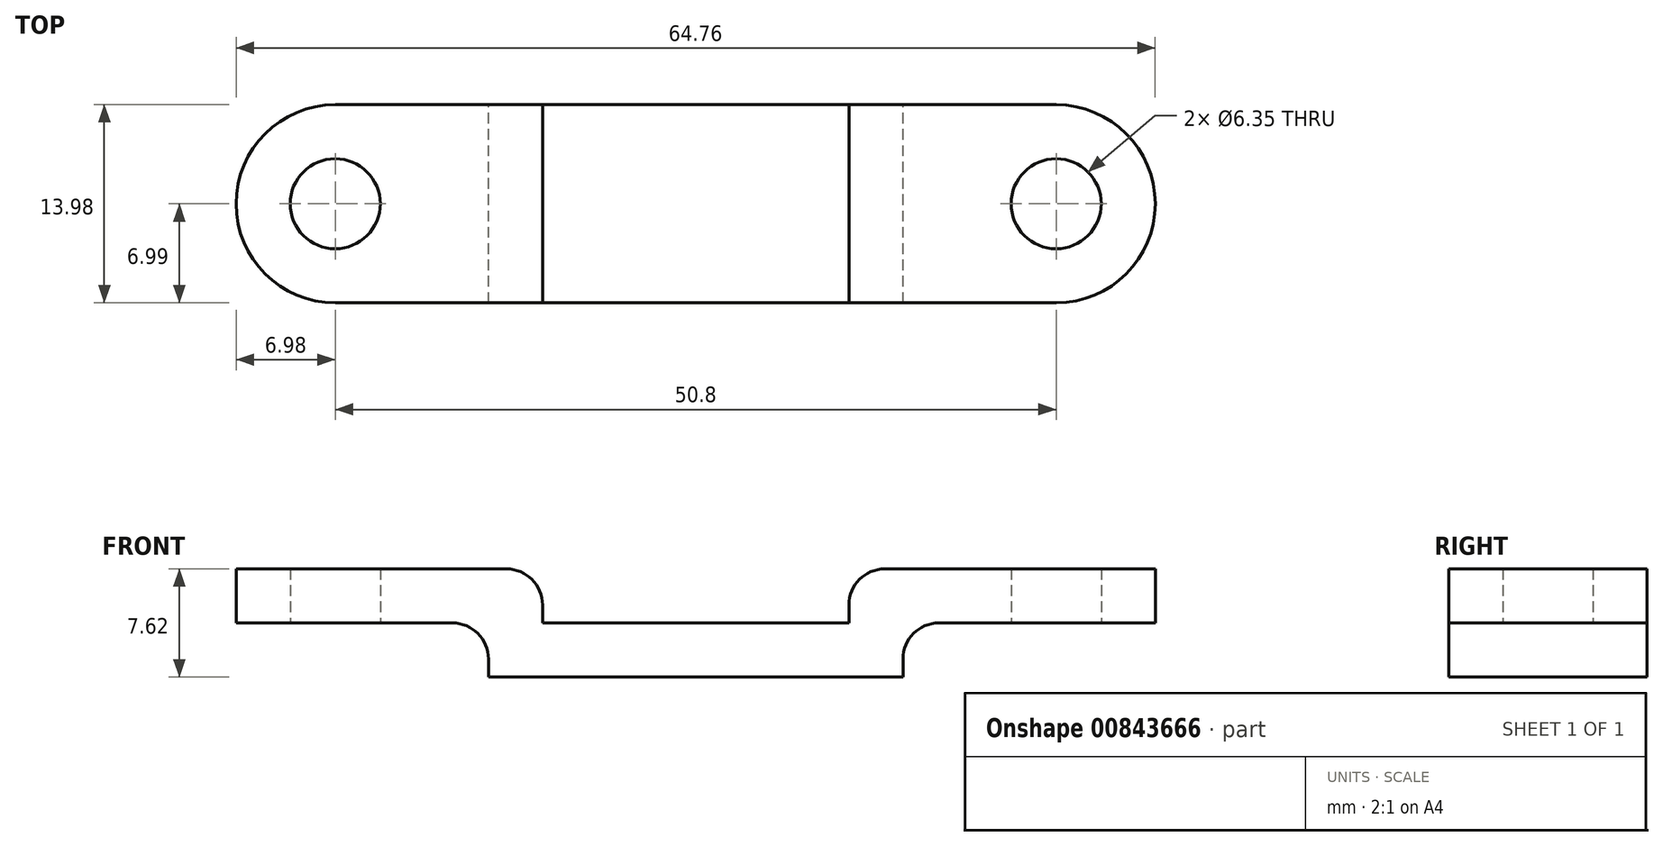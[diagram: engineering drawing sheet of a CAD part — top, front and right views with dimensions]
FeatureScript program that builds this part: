
annotation { "Feature Type Name" : "Feature", "Feature Type Description" : "" }
export const myFeature = defineFeature(function(context is Context, id is Id, definition is map)
    precondition{}
    {
        {
            var Q0;
            Q0=qCreatedBy(makeId("Top.planeOp"),FACE);
            var sketch = newSketch(context, id + "F0", { "sketchPlane" : qUnion([Q0])});
            skLineSegment(sketch, "E0.bottom", {"start": v(25.4, 6.99) * mm, "end": v(-25.4, 6.99) * mm});
            skLineSegment(sketch, "E0.top", {"start": v(25.4, -6.98) * mm, "end": v(-25.4, -6.98) * mm});
            skPoint(sketch, "E0.middle", {"position": v(0, 0) * mm});
            skArc(sketch, "E1", {"start": v(-25.4, 6.99) * mm, "mid": v(-32.38, 0) * mm, "end": v(-25.4, -6.98) * mm});
            skArc(sketch, "E2", {"start": v(25.4, -6.98) * mm, "mid": v(32.39, 0) * mm, "end": v(25.4, 6.99) * mm});
            skCircle(sketch, "E3", {"center": v(-25.4, 0) * mm, "radius": 3.18 * mm});
            skCircle(sketch, "E4", {"center": v(25.4, 0) * mm, "radius": 3.18 * mm});
            skLineSegment(sketch, "E5.bottom", {"start": v(-10.8, 6.99) * mm, "end": v(10.8, 6.99) * mm, "construction": true});
            skLineSegment(sketch, "E5.top", {"start": v(-10.8, -6.99) * mm, "end": v(10.8, -6.99) * mm, "construction": true});
            skLineSegment(sketch, "E5.left", {"start": v(-10.8, 6.99) * mm, "end": v(-10.8, -6.99) * mm, "construction": true});
            skLineSegment(sketch, "E5.right", {"start": v(10.8, 6.99) * mm, "end": v(10.8, -6.99) * mm, "construction": true});
            skSolve(sketch);
        }
        {
            var Q0;
            Q0 = qSketchRegion(id + "F0", true);
            extrude(context, id + "F1", {"entities" : qUnion([Q0]), "depth" : 7.62 * mm / 2, "offsetDistance" : 25.4 * mm});
        }
        {
            var Q0;
            Q0=makeQuery(id+"F1.opExtrude","CAP_FACE",FACE,{"disambiguationData":[OSD([sQuery(id+"F0.wireOp",EDGE,"E0.bottom"),sQuery(id+"F0.wireOp",EDGE,"E0.top"),sQuery(id+"F0.wireOp",EDGE,"E1"),sQuery(id+"F0.wireOp",EDGE,"E2"),sQuery(id+"F0.wireOp",EDGE,"E3"),sQuery(id+"F0.wireOp",EDGE,"E4")])],"isStart":false});
            var sketch = newSketch(context, id + "F2", { "sketchPlane" : qUnion([Q0])});
            skLineSegment(sketch, "E6.0", {"start": v(-10.8, 6.99) * mm, "end": v(-10.8, -6.99) * mm});
            skCircle(sketch, "E7.0", {"center": v(-25.4, 0) * mm, "radius": 3.18 * mm});
            skArc(sketch, "E8.0", {"start": v(-25.4, 6.99) * mm, "mid": v(-32.38, 0) * mm, "end": v(-25.4, -6.98) * mm});
            skLineSegment(sketch, "E9.0", {"start": v(-10.8, 6.99) * mm, "end": v(-25.4, 6.99) * mm});
            skLineSegment(sketch, "E10.0", {"start": v(-10.8, -6.98) * mm, "end": v(-25.4, -6.98) * mm});
            skSolve(sketch);
        }
        {
            var Q0;
            Q0=makeQuery(id+"F2.imprint","IMPRINT",FACE,{"disambiguationData":[TD([[makeQuery(id+"F2.imprint","IMPRINT",EDGE,{"derivedFrom":sQuery(id+"F2.wireOp",EDGE,"E6.0")}),-1.0]])]});
            extrude(context, id + "F3", {"entities" : qUnion([Q0]), "operationType" : NewBodyOperationType.ADD, "depth" : 7.62 * mm / 2, "offsetDistance" : 25.4 * mm});
        }
        {
            var Q0;
            Q0=makeQuery(id+"F3.boolean.opBoolean","MERGE",FACE,{"derivedFrom":[makeQuery(id+"F1.opExtrude","SWEPT_FACE",FACE,{"disambiguationData":[OSD([sQuery(id+"F0.wireOp",EDGE,"E0.bottom")])]}),makeQuery(id+"F3.opExtrude","SWEPT_FACE",FACE,{"disambiguationData":[OSD([sQuery(id+"F2.wireOp",EDGE,"E9.0")])]})]});
            var sketch = newSketch(context, id + "F4", { "sketchPlane" : qUnion([Q0])});
            skLineSegment(sketch, "E11.bottom", {"start": v(14.6, 0) * mm, "end": v(60.73, 0) * mm});
            skLineSegment(sketch, "E11.top", {"start": v(14.6, 3.81) * mm, "end": v(60.73, 3.81) * mm});
            skLineSegment(sketch, "E11.left", {"start": v(14.6, 0) * mm, "end": v(14.6, 3.81) * mm});
            skLineSegment(sketch, "E11.right", {"start": v(60.73, 0) * mm, "end": v(60.73, 3.81) * mm});
            skSolve(sketch);
        }
        {
            var Q0;
            {var subQ3=sQuery(id+"F4.wireOp",EDGE,"E11.right");Q0=makeQuery(id+"F4.imprint","IMPRINT",FACE,{"disambiguationData":[TD([[makeQuery(id+"F4.imprint","IMPRINT",EDGE,{"derivedFrom":subQ3}),1.0]])]});}
            var Q1;
            {var subQ4=sQuery(id+"F4.wireOp",EDGE,"E11.left");Q1=makeQuery(id+"F4.imprint","IMPRINT",FACE,{"disambiguationData":[TD([[makeQuery(id+"F4.imprint","IMPRINT",EDGE,{"derivedFrom":subQ4}),-1.0]])]});}
            extrude(context, id + "F5", {"entities" : qUnion([Q0, Q1]), "operationType" : NewBodyOperationType.REMOVE, "oppositeDirection" : true, "depth" : 38.1 * mm, "offsetDistance" : 25.4 * mm});
        }
        {
            var Q0;
            Q0=makeQuery(id+"F3.opExtrude","CAP_EDGE",EDGE,{"disambiguationData":[OSD([sQuery(id+"F2.wireOp",EDGE,"E6.0")])],"isStart":true});
            var Q1;
            Q1=makeQuery(id+"F5.boolean.opBoolean","COPY",EDGE,{"derivedFrom":makeQuery(id+"F5.opExtrude","SWEPT_EDGE",EDGE,{"disambiguationData":[OSD([sQuery(id+"F4.wireOp",EDGE,"E11.top"),sQuery(id+"F4.wireOp",EDGE,"E11.left")])]})});
            fillet(context, id + "F6", {"entities" : qUnion([Q0, Q1]), "radius" : 2.54 * mm, "tangentPropagation" : true, "allowEdgeOverflow" : false});
        }
        {
            var Q0;
            Q0=makeQuery(id+"F3.opExtrude","CAP_EDGE",EDGE,{"disambiguationData":[OSD([sQuery(id+"F2.wireOp",EDGE,"E6.0")])],"isStart":false});
            var Q1;
            Q1=makeQuery(id+"F5.boolean.opBoolean","COPY",EDGE,{"derivedFrom":makeQuery(id+"F5.opExtrude","SWEPT_EDGE",EDGE,{"disambiguationData":[OSD([sQuery(id+"F0.wireOp",EDGE,"E0.bottom"),sQuery(id+"F4.wireOp",EDGE,"E11.bottom"),sQuery(id+"F4.wireOp",EDGE,"E11.left")])]})});
            var Q2;
            Q2=makeQuery(id+"F6.opFillet","BLEND_EDGE",EDGE,{"blendedFrom":[makeQuery(id+"F5.boolean.opBoolean","COPY",EDGE,{"derivedFrom":makeQuery(id+"F5.opExtrude","SWEPT_EDGE",EDGE,{"disambiguationData":[OSD([sQuery(id+"F4.wireOp",EDGE,"E11.top"),sQuery(id+"F4.wireOp",EDGE,"E11.left")])]})}),makeQuery(id+"F1.opExtrude","CAP_FACE",FACE,{"disambiguationData":[OSD([sQuery(id+"F0.wireOp",EDGE,"E0.bottom"),sQuery(id+"F0.wireOp",EDGE,"E0.top"),sQuery(id+"F0.wireOp",EDGE,"E1"),sQuery(id+"F0.wireOp",EDGE,"E2"),sQuery(id+"F0.wireOp",EDGE,"E3"),sQuery(id+"F0.wireOp",EDGE,"E4")])],"isStart":true})],"blendedInto":[makeQuery(id+"F1.opExtrude","CAP_FACE",FACE,{"disambiguationData":[OSD([sQuery(id+"F0.wireOp",EDGE,"E0.bottom"),sQuery(id+"F0.wireOp",EDGE,"E0.top"),sQuery(id+"F0.wireOp",EDGE,"E1"),sQuery(id+"F0.wireOp",EDGE,"E2"),sQuery(id+"F0.wireOp",EDGE,"E3"),sQuery(id+"F0.wireOp",EDGE,"E4")])],"isStart":true})]});
            var Q3;
            {var subQ0=sQuery(id+"F2.wireOp",EDGE,"E6.0");Q3=makeQuery(id+"F6.opFillet","BLEND_EDGE",EDGE,{"blendedFrom":[makeQuery(id+"F3.opExtrude","CAP_EDGE",EDGE,{"disambiguationData":[OSD([subQ0])],"isStart":true}),makeQuery(id+"F3.opExtrude","CAP_FACE",FACE,{"disambiguationData":[OSD([subQ0,sQuery(id+"F2.wireOp",EDGE,"E7.0"),sQuery(id+"F2.wireOp",EDGE,"E8.0"),sQuery(id+"F2.wireOp",EDGE,"E9.0"),sQuery(id+"F2.wireOp",EDGE,"E10.0")])],"isStart":false})],"blendedInto":[makeQuery(id+"F3.opExtrude","CAP_FACE",FACE,{"disambiguationData":[OSD([subQ0,sQuery(id+"F2.wireOp",EDGE,"E7.0"),sQuery(id+"F2.wireOp",EDGE,"E8.0"),sQuery(id+"F2.wireOp",EDGE,"E9.0"),sQuery(id+"F2.wireOp",EDGE,"E10.0")])],"isStart":false})]});}
            fillet(context, id + "F7", {"entities" : qUnion([Q0, Q1, Q2, Q3]), "radius" : 2.54 * mm, "tangentPropagation" : true, "allowEdgeOverflow" : false});
        }
        {
            var Q0;
            Q0=makeQuery(id+"F1.opExtrude","CAP_FACE",FACE,{"disambiguationData":[OSD([sQuery(id+"F0.wireOp",EDGE,"E0.bottom"),sQuery(id+"F0.wireOp",EDGE,"E0.top"),sQuery(id+"F0.wireOp",EDGE,"E1"),sQuery(id+"F0.wireOp",EDGE,"E2"),sQuery(id+"F0.wireOp",EDGE,"E3"),sQuery(id+"F0.wireOp",EDGE,"E4")])],"isStart":false});
            var sketch = newSketch(context, id + "F8", { "sketchPlane" : qUnion([Q0])});
            skLineSegment(sketch, "E12.0", {"start": v(10.8, 6.99) * mm, "end": v(10.8, -6.99) * mm});
            skLineSegment(sketch, "E13.0.0", {"start": v(25.4, 6.99) * mm, "end": v(10.8, 6.99) * mm});
            skLineSegment(sketch, "E13.0.2", {"start": v(10.8, -6.98) * mm, "end": v(25.4, -6.98) * mm});
            skArc(sketch, "E13.0.3", {"start": v(25.4, -6.98) * mm, "mid": v(32.39, 0) * mm, "end": v(25.4, 6.99) * mm});
            skCircle(sketch, "E14.0", {"center": v(25.4, 0) * mm, "radius": 3.18 * mm});
            skPoint(sketch, "E13.0.1.end.orphan", {"position": v(-8.26, -6.98) * mm});
            skPoint(sketch, "E13.0.1.start.orphan", {"position": v(-8.26, 6.99) * mm});
            skSolve(sketch);
        }
        {
            var Q0;
            Q0 = qSketchRegion(id + "F8", true);
            extrude(context, id + "F9", {"entities" : qUnion([Q0]), "operationType" : NewBodyOperationType.ADD, "depth" : 7.62 * mm / 2, "offsetDistance" : 25.4 * mm});
        }
        {
            var Q0;
            Q0=makeQuery(id+"F9.boolean.opBoolean","MERGE",FACE,{"derivedFrom":[makeQuery(id+"F3.boolean.opBoolean","MERGE",FACE,{"derivedFrom":[makeQuery(id+"F1.opExtrude","SWEPT_FACE",FACE,{"disambiguationData":[OSD([sQuery(id+"F0.wireOp",EDGE,"E0.bottom")])]}),makeQuery(id+"F3.opExtrude","SWEPT_FACE",FACE,{"disambiguationData":[OSD([sQuery(id+"F2.wireOp",EDGE,"E9.0")])]})]}),makeQuery(id+"F9.opExtrude","SWEPT_FACE",FACE,{"disambiguationData":[OSD([sQuery(id+"F8.wireOp",EDGE,"E13.0.0")])]})]});
            var sketch = newSketch(context, id + "F10", { "sketchPlane" : qUnion([Q0])});
            skLineSegment(sketch, "E15.bottom", {"start": v(-14.6, 0) * mm, "end": v(-33.66, 0) * mm});
            skLineSegment(sketch, "E15.top", {"start": v(-14.6, 3.81) * mm, "end": v(-33.66, 3.81) * mm});
            skLineSegment(sketch, "E15.left", {"start": v(-14.6, 0) * mm, "end": v(-14.6, 3.8) * mm});
            skLineSegment(sketch, "E15.right", {"start": v(-33.66, 0) * mm, "end": v(-33.66, 3.81) * mm});
            skSolve(sketch);
        }
        {
            var Q0;
            Q0 = qSketchRegion(id + "F10", true);
            extrude(context, id + "F11", {"entities" : qUnion([Q0]), "operationType" : NewBodyOperationType.REMOVE, "oppositeDirection" : true, "depth" : 38.1 * mm, "offsetDistance" : 25.4 * mm});
        }
        {
            var Q0;
            Q0=makeQuery(id+"F11.boolean.opBoolean","COPY",EDGE,{"derivedFrom":makeQuery(id+"F11.opExtrude","SWEPT_EDGE",EDGE,{"disambiguationData":[OSD([sQuery(id+"F0.wireOp",EDGE,"E0.bottom"),sQuery(id+"F10.wireOp",EDGE,"E15.bottom"),sQuery(id+"F10.wireOp",EDGE,"E15.left")])]})});
            var Q1;
            Q1=makeQuery(id+"F9.opExtrude","CAP_EDGE",EDGE,{"disambiguationData":[OSD([sQuery(id+"F8.wireOp",EDGE,"E12.0")])],"isStart":false});
            fillet(context, id + "F12", {"entities" : qUnion([Q0, Q1]), "radius" : 5.08 * mm / 2, "tangentPropagation" : true, "allowEdgeOverflow" : false});
        }
        {
            var Q0;
            Q0=makeQuery(id+"F9.opExtrude","CAP_EDGE",EDGE,{"disambiguationData":[OSD([sQuery(id+"F8.wireOp",EDGE,"E12.0")])],"isStart":true});
            var Q1;
            Q1=makeQuery(id+"F11.boolean.opBoolean","COPY",EDGE,{"derivedFrom":makeQuery(id+"F11.opExtrude","SWEPT_EDGE",EDGE,{"disambiguationData":[OSD([sQuery(id+"F10.wireOp",EDGE,"E15.top"),sQuery(id+"F10.wireOp",EDGE,"E15.left")])]})});
            fillet(context, id + "F13", {"entities" : qUnion([Q0, Q1]), "radius" : 5.08 * mm / 2, "tangentPropagation" : true, "allowEdgeOverflow" : false});
        }
    });
